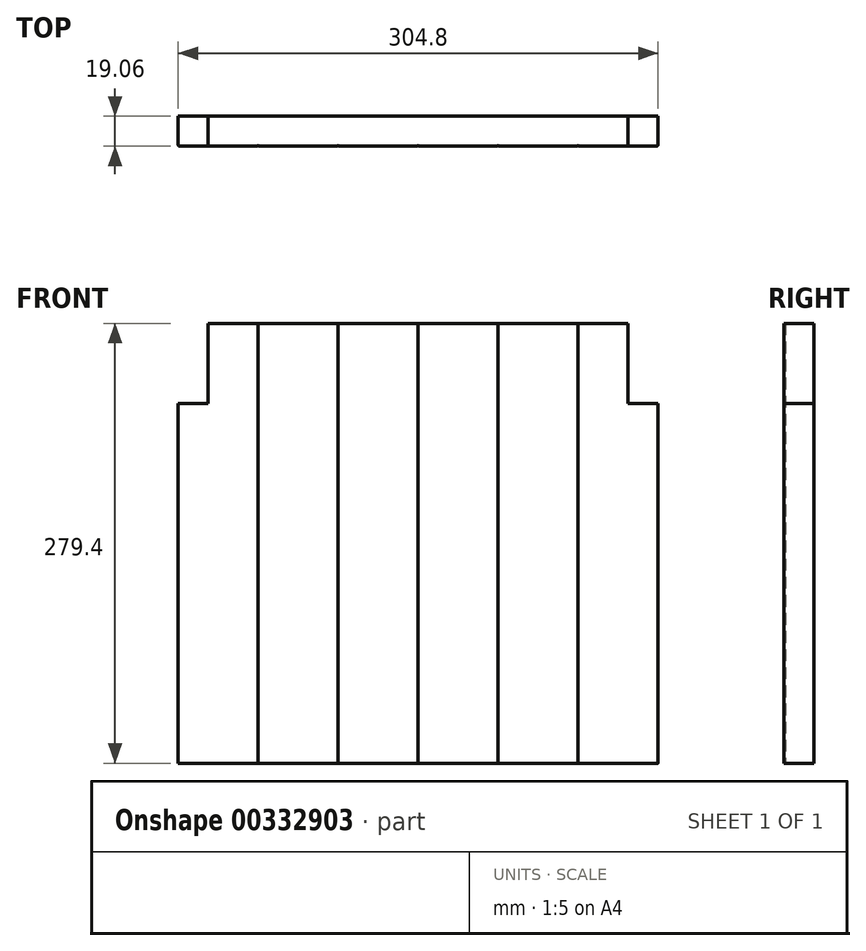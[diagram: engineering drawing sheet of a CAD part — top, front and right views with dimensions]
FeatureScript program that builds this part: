
annotation { "Feature Type Name" : "Feature", "Feature Type Description" : "" }
export const myFeature = defineFeature(function(context is Context, id is Id, definition is map)
    precondition{}
    {
        {
            var Q0;
            Q0=qCreatedBy(makeId("Top.planeOp"),FACE);
            var sketch = newSketch(context, id + "F0", { "sketchPlane" : qUnion([Q0])});
            skLineSegment(sketch, "E0.bottom", {"start": v(533.4, -9.53) * mm, "end": v(458.22, -9.53) * mm});
            skLineSegment(sketch, "E0.top", {"start": v(533.4, 9.53) * mm, "end": v(-533.4, 9.53) * mm});
            skLineSegment(sketch, "E0.left", {"start": v(533.4, 9.53) * mm, "end": v(533.4, -9.53) * mm});
            skLineSegment(sketch, "E0.right", {"start": v(-533.4, 9.53) * mm, "end": v(-533.4, -9.53) * mm});
            skPoint(sketch, "E0.middle", {"position": v(0, 0) * mm});
            skArc(sketch, "E1", {"start": v(-509.02, -9.53) * mm, "mid": v(-508.3, -9.23) * mm, "end": v(-508, -8.5) * mm});
            skArc(sketch, "E2", {"start": v(-508, -8.5) * mm, "mid": v(-507.7, -9.23) * mm, "end": v(-506.98, -9.52) * mm});
            skArc(sketch, "E3.1.0.0", {"start": v(-458.22, -9.53) * mm, "mid": v(-457.5, -9.23) * mm, "end": v(-457.2, -8.5) * mm});
            skArc(sketch, "E3.1.0.1", {"start": v(-457.2, -8.5) * mm, "mid": v(-456.9, -9.23) * mm, "end": v(-456.18, -9.52) * mm});
            skArc(sketch, "E3.2.0.0", {"start": v(-407.42, -9.53) * mm, "mid": v(-406.7, -9.23) * mm, "end": v(-406.4, -8.5) * mm});
            skArc(sketch, "E3.2.0.1", {"start": v(-406.4, -8.5) * mm, "mid": v(-406.1, -9.23) * mm, "end": v(-405.38, -9.52) * mm});
            skArc(sketch, "E3.3.0.0", {"start": v(-356.62, -9.53) * mm, "mid": v(-355.9, -9.23) * mm, "end": v(-355.6, -8.5) * mm});
            skArc(sketch, "E3.3.0.1", {"start": v(-355.6, -8.5) * mm, "mid": v(-355.3, -9.23) * mm, "end": v(-354.58, -9.52) * mm});
            skArc(sketch, "E3.4.0.0", {"start": v(-305.82, -9.53) * mm, "mid": v(-305.1, -9.23) * mm, "end": v(-304.8, -8.5) * mm});
            skArc(sketch, "E3.4.0.1", {"start": v(-304.8, -8.5) * mm, "mid": v(-304.5, -9.23) * mm, "end": v(-303.78, -9.52) * mm});
            skArc(sketch, "E3.5.0.0", {"start": v(-255.02, -9.53) * mm, "mid": v(-254.3, -9.23) * mm, "end": v(-254, -8.5) * mm});
            skArc(sketch, "E3.5.0.1", {"start": v(-254, -8.5) * mm, "mid": v(-253.7, -9.23) * mm, "end": v(-252.98, -9.52) * mm});
            skArc(sketch, "E3.6.0.0", {"start": v(-204.22, -9.53) * mm, "mid": v(-203.5, -9.23) * mm, "end": v(-203.2, -8.5) * mm});
            skArc(sketch, "E3.6.0.1", {"start": v(-203.2, -8.5) * mm, "mid": v(-202.9, -9.23) * mm, "end": v(-202.18, -9.52) * mm});
            skArc(sketch, "E3.7.0.0", {"start": v(-153.42, -9.53) * mm, "mid": v(-152.7, -9.23) * mm, "end": v(-152.4, -8.5) * mm});
            skArc(sketch, "E3.7.0.1", {"start": v(-152.4, -8.5) * mm, "mid": v(-152.1, -9.23) * mm, "end": v(-151.38, -9.52) * mm});
            skArc(sketch, "E3.8.0.0", {"start": v(-102.62, -9.53) * mm, "mid": v(-101.9, -9.23) * mm, "end": v(-101.6, -8.5) * mm});
            skArc(sketch, "E3.8.0.1", {"start": v(-101.6, -8.5) * mm, "mid": v(-101.3, -9.23) * mm, "end": v(-100.58, -9.52) * mm});
            skArc(sketch, "E3.9.0.0", {"start": v(-51.82, -9.53) * mm, "mid": v(-51.1, -9.23) * mm, "end": v(-50.8, -8.5) * mm});
            skArc(sketch, "E3.9.0.1", {"start": v(-50.8, -8.5) * mm, "mid": v(-50.5, -9.23) * mm, "end": v(-49.78, -9.52) * mm});
            skArc(sketch, "E3.10.0.0", {"start": v(-1.02, -9.53) * mm, "mid": v(-0.3, -9.23) * mm, "end": v(0, -8.5) * mm});
            skArc(sketch, "E3.10.0.1", {"start": v(0, -8.5) * mm, "mid": v(0.3, -9.23) * mm, "end": v(1.02, -9.52) * mm});
            skArc(sketch, "E3.11.0.0", {"start": v(49.78, -9.53) * mm, "mid": v(50.5, -9.23) * mm, "end": v(50.8, -8.5) * mm});
            skArc(sketch, "E3.11.0.1", {"start": v(50.8, -8.5) * mm, "mid": v(51.1, -9.23) * mm, "end": v(51.82, -9.52) * mm});
            skArc(sketch, "E3.12.0.0", {"start": v(100.58, -9.53) * mm, "mid": v(101.3, -9.23) * mm, "end": v(101.6, -8.5) * mm});
            skArc(sketch, "E3.12.0.1", {"start": v(101.6, -8.5) * mm, "mid": v(101.9, -9.23) * mm, "end": v(102.62, -9.52) * mm});
            skArc(sketch, "E3.13.0.0", {"start": v(151.38, -9.53) * mm, "mid": v(152.1, -9.23) * mm, "end": v(152.4, -8.5) * mm});
            skArc(sketch, "E3.13.0.1", {"start": v(152.4, -8.5) * mm, "mid": v(152.7, -9.23) * mm, "end": v(153.42, -9.52) * mm});
            skArc(sketch, "E3.14.0.0", {"start": v(202.18, -9.53) * mm, "mid": v(202.9, -9.23) * mm, "end": v(203.2, -8.5) * mm});
            skArc(sketch, "E3.14.0.1", {"start": v(203.2, -8.5) * mm, "mid": v(203.5, -9.23) * mm, "end": v(204.22, -9.52) * mm});
            skArc(sketch, "E3.15.0.0", {"start": v(252.98, -9.53) * mm, "mid": v(253.7, -9.23) * mm, "end": v(254, -8.5) * mm});
            skArc(sketch, "E3.15.0.1", {"start": v(254, -8.5) * mm, "mid": v(254.3, -9.23) * mm, "end": v(255.02, -9.52) * mm});
            skArc(sketch, "E3.16.0.0", {"start": v(303.78, -9.53) * mm, "mid": v(304.5, -9.23) * mm, "end": v(304.8, -8.5) * mm});
            skArc(sketch, "E3.16.0.1", {"start": v(304.8, -8.5) * mm, "mid": v(305.1, -9.23) * mm, "end": v(305.82, -9.52) * mm});
            skArc(sketch, "E3.17.0.0", {"start": v(354.58, -9.53) * mm, "mid": v(355.3, -9.23) * mm, "end": v(355.6, -8.5) * mm});
            skArc(sketch, "E3.17.0.1", {"start": v(355.6, -8.5) * mm, "mid": v(355.9, -9.23) * mm, "end": v(356.62, -9.52) * mm});
            skArc(sketch, "E3.18.0.0", {"start": v(405.38, -9.53) * mm, "mid": v(406.1, -9.23) * mm, "end": v(406.4, -8.5) * mm});
            skArc(sketch, "E3.18.0.1", {"start": v(406.4, -8.5) * mm, "mid": v(406.7, -9.23) * mm, "end": v(407.42, -9.52) * mm});
            skArc(sketch, "E3.19.0.0", {"start": v(456.18, -9.53) * mm, "mid": v(456.9, -9.23) * mm, "end": v(457.2, -8.5) * mm});
            skArc(sketch, "E3.19.0.1", {"start": v(457.2, -8.5) * mm, "mid": v(457.5, -9.23) * mm, "end": v(458.22, -9.52) * mm});
            skLineSegment(sketch, "E3.direction1", {"start": v(-506.98, -9.53) * mm, "end": v(-458.22, -9.53) * mm, "construction": true});
            skLineSegment(sketch, "E4.trimOffspring", {"start": v(-458.22, -9.53) * mm, "end": v(-533.4, -9.53) * mm});
            skLineSegment(sketch, "E5.trimOffspring", {"start": v(-407.42, -9.53) * mm, "end": v(-456.18, -9.53) * mm});
            skLineSegment(sketch, "E6.trimOffspring", {"start": v(-356.62, -9.53) * mm, "end": v(-405.38, -9.53) * mm});
            skLineSegment(sketch, "E7.trimOffspring", {"start": v(-305.82, -9.53) * mm, "end": v(-354.58, -9.53) * mm});
            skLineSegment(sketch, "E8.trimOffspring", {"start": v(-255.02, -9.53) * mm, "end": v(-303.78, -9.53) * mm});
            skLineSegment(sketch, "E9.trimOffspring", {"start": v(-204.22, -9.53) * mm, "end": v(-252.98, -9.53) * mm});
            skLineSegment(sketch, "E10.trimOffspring", {"start": v(-153.42, -9.53) * mm, "end": v(-202.18, -9.53) * mm});
            skLineSegment(sketch, "E11.trimOffspring", {"start": v(-102.62, -9.53) * mm, "end": v(-151.38, -9.53) * mm});
            skLineSegment(sketch, "E12.trimOffspring", {"start": v(-51.82, -9.53) * mm, "end": v(-100.58, -9.53) * mm});
            skLineSegment(sketch, "E13.trimOffspring", {"start": v(-1.02, -9.53) * mm, "end": v(-49.78, -9.53) * mm});
            skLineSegment(sketch, "E14.trimOffspring", {"start": v(49.78, -9.53) * mm, "end": v(1.02, -9.53) * mm});
            skLineSegment(sketch, "E15.trimOffspring", {"start": v(100.58, -9.53) * mm, "end": v(51.82, -9.53) * mm});
            skLineSegment(sketch, "E16.trimOffspring", {"start": v(151.38, -9.53) * mm, "end": v(102.62, -9.53) * mm});
            skLineSegment(sketch, "E17.trimOffspring", {"start": v(202.18, -9.53) * mm, "end": v(153.42, -9.53) * mm});
            skLineSegment(sketch, "E18.trimOffspring", {"start": v(252.98, -9.53) * mm, "end": v(204.22, -9.53) * mm});
            skLineSegment(sketch, "E19.trimOffspring", {"start": v(303.78, -9.53) * mm, "end": v(255.02, -9.53) * mm});
            skLineSegment(sketch, "E20.trimOffspring", {"start": v(354.58, -9.53) * mm, "end": v(305.82, -9.53) * mm});
            skLineSegment(sketch, "E21.trimOffspring", {"start": v(405.38, -9.53) * mm, "end": v(356.62, -9.53) * mm});
            skLineSegment(sketch, "E22.trimOffspring", {"start": v(456.18, -9.53) * mm, "end": v(407.42, -9.53) * mm});
            skSolve(sketch);
        }
        {
            var Q0;
            Q0=qSketchRegion(id+"F0",true);
            extrude(context, id + "F1", {"entities" : qUnion([Q0]), "depth" : 279.4 * mm});
        }
        {
            var Q0;
            Q0=qCreatedBy(makeId("Top.planeOp"),FACE);
            var sketch = newSketch(context, id + "F2", { "sketchPlane" : qUnion([Q0])});
            skLineSegment(sketch, "E23.bottom", {"start": v(-660.4, -213.36) * mm, "end": v(-152.4, -213.36) * mm});
            skLineSegment(sketch, "E23.top", {"start": v(-660.4, 213.36) * mm, "end": v(-152.4, 213.36) * mm});
            skLineSegment(sketch, "E23.left", {"start": v(-660.4, -213.36) * mm, "end": v(-660.4, 213.36) * mm});
            skLineSegment(sketch, "E23.right", {"start": v(-152.4, -213.36) * mm, "end": v(-152.4, 213.36) * mm});
            skPoint(sketch, "E23.middle", {"position": v(-406.4, 0) * mm});
            skLineSegment(sketch, "E24.bottom", {"start": v(660.4, 55.53) * mm, "end": v(152.4, 55.53) * mm});
            skLineSegment(sketch, "E24.top", {"start": v(660.4, -55.53) * mm, "end": v(152.4, -55.53) * mm});
            skLineSegment(sketch, "E24.left", {"start": v(660.4, 55.53) * mm, "end": v(660.4, -55.53) * mm});
            skLineSegment(sketch, "E24.right", {"start": v(152.4, 55.53) * mm, "end": v(152.4, -55.53) * mm});
            skPoint(sketch, "E24.middle", {"position": v(406.4, 0) * mm});
            skSolve(sketch);
        }
        {
            var Q0;
            Q0 = qSketchRegion(id + "F2", true);
            extrude(context, id + "F3", {"entities" : qUnion([Q0]), "operationType" : NewBodyOperationType.REMOVE, "endBound" : BoundingType.SYMMETRIC, "oppositeDirection" : true, "depth" : 609.6 * mm});
        }
        {
            var Q0;
            Q0=qCreatedBy(makeId("Front.planeOp"),FACE);
            var sketch = newSketch(context, id + "F4", { "sketchPlane" : qUnion([Q0])});
            skLineSegment(sketch, "E25.bottom", {"start": v(152.4, 279.4) * mm, "end": v(133.35, 279.4) * mm});
            skLineSegment(sketch, "E25.top", {"start": v(152.4, 228.6) * mm, "end": v(133.35, 228.6) * mm});
            skLineSegment(sketch, "E25.left", {"start": v(152.4, 279.4) * mm, "end": v(152.4, 228.6) * mm});
            skLineSegment(sketch, "E25.right", {"start": v(133.35, 279.4) * mm, "end": v(133.35, 228.6) * mm});
            skLineSegment(sketch, "E26.bottom", {"start": v(-152.4, 279.4) * mm, "end": v(-133.35, 279.4) * mm});
            skLineSegment(sketch, "E26.top", {"start": v(-152.4, 228.6) * mm, "end": v(-133.35, 228.6) * mm});
            skLineSegment(sketch, "E26.left", {"start": v(-152.4, 279.4) * mm, "end": v(-152.4, 228.6) * mm});
            skLineSegment(sketch, "E26.right", {"start": v(-133.35, 279.4) * mm, "end": v(-133.35, 228.6) * mm});
            skSolve(sketch);
        }
        {
            var Q0;
            Q0 = qSketchRegion(id + "F4", true);
            extrude(context, id + "F5", {"entities" : qUnion([Q0]), "operationType" : NewBodyOperationType.REMOVE, "endBound" : BoundingType.SYMMETRIC, "oppositeDirection" : true, "depth" : 25.4 * mm});
        }
    });
